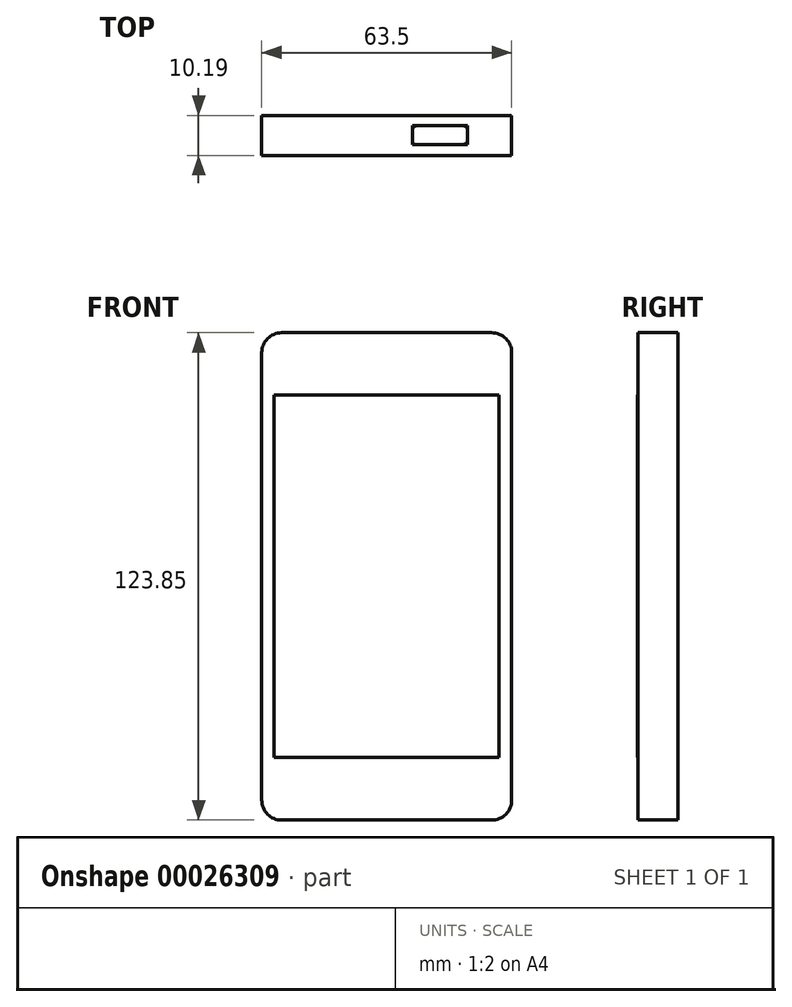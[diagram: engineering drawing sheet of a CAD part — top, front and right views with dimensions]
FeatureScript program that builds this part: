
annotation { "Feature Type Name" : "Feature", "Feature Type Description" : "" }
export const myFeature = defineFeature(function(context is Context, id is Id, definition is map)
    precondition{}
    {
        {
            var Q0;
            Q0=qCreatedBy(makeId("Front.planeOp"),FACE);
            var sketch = newSketch(context, id + "F0", { "sketchPlane" : qUnion([Q0])});
            skLineSegment(sketch, "E0.bottom", {"start": v(-42.36, 75.13) * mm, "end": v(21.14, 75.13) * mm});
            skLineSegment(sketch, "E0.top", {"start": v(-42.36, -48.7) * mm, "end": v(21.14, -48.7) * mm});
            skLineSegment(sketch, "E0.left", {"start": v(-42.36, 75.13) * mm, "end": v(-42.36, -48.7) * mm});
            skLineSegment(sketch, "E0.right", {"start": v(21.14, 75.13) * mm, "end": v(21.14, -48.7) * mm});
            skSolve(sketch);
        }
        {
            var Q0;
            Q0 = qSketchRegion(id + "F0", true);
            extrude(context, id + "F1", {"entities" : qUnion([Q0]), "depth" : 10.16 * mm});
        }
        {
            var Q0;
            Q0=makeQuery(id+"F1.opExtrude","SWEPT_EDGE",EDGE,{"disambiguationData":[OSD([sQuery(id+"F0.wireOp",EDGE,"E0.bottom"),sQuery(id+"F0.wireOp",EDGE,"E0.left")])]});
            var Q1;
            Q1=makeQuery(id+"F1.opExtrude","SWEPT_EDGE",EDGE,{"disambiguationData":[OSD([sQuery(id+"F0.wireOp",EDGE,"E0.bottom"),sQuery(id+"F0.wireOp",EDGE,"E0.right")])]});
            var Q2;
            Q2=makeQuery(id+"F1.opExtrude","SWEPT_EDGE",EDGE,{"disambiguationData":[OSD([sQuery(id+"F0.wireOp",EDGE,"E0.top"),sQuery(id+"F0.wireOp",EDGE,"E0.right")])]});
            fillet(context, id + "F2", {"entities" : qUnion([Q0, Q1, Q2]), "radius" : 5.08 * mm, "tangentPropagation" : true, "allowEdgeOverflow" : false});
        }
        {
            var Q0;
            Q0=makeQuery(id+"F1.opExtrude","SWEPT_EDGE",EDGE,{"disambiguationData":[OSD([sQuery(id+"F0.wireOp",EDGE,"E0.top"),sQuery(id+"F0.wireOp",EDGE,"E0.left")])]});
            fillet(context, id + "F3", {"entities" : qUnion([Q0]), "radius" : 5.08 * mm, "tangentPropagation" : true, "allowEdgeOverflow" : false});
        }
        {
            var Q0;
            Q0=makeQuery(id+"F1.opExtrude","CAP_FACE",FACE,{"disambiguationData":[OSD([sQuery(id+"F0.wireOp",EDGE,"E0.bottom"),sQuery(id+"F0.wireOp",EDGE,"E0.top"),sQuery(id+"F0.wireOp",EDGE,"E0.left"),sQuery(id+"F0.wireOp",EDGE,"E0.right")])],"isStart":false});
            var sketch = newSketch(context, id + "F4", { "sketchPlane" : qUnion([Q0])});
            skLineSegment(sketch, "E1.0", {"start": v(-39.18, 59.25) * mm, "end": v(17.97, 59.25) * mm});
            skLineSegment(sketch, "E2.0", {"start": v(17.97, 59.25) * mm, "end": v(17.97, -32.82) * mm});
            skLineSegment(sketch, "E3.0", {"start": v(-39.18, 59.25) * mm, "end": v(-39.18, -32.82) * mm});
            skLineSegment(sketch, "E4.0", {"start": v(-39.18, -32.82) * mm, "end": v(17.97, -32.82) * mm});
            skSolve(sketch);
        }
        {
            var Q0;
            Q0=makeQuery(id+"F4.imprint","IMPRINT",FACE,{"disambiguationData":[TD([[makeQuery(id+"F4.imprint","IMPRINT",EDGE,{"derivedFrom":sQuery(id+"F4.wireOp",EDGE,"E1.0")}),-1.0]])]});
            extrude(context, id + "F5", {"entities" : qUnion([Q0]), "depth" : 0.03 * mm});
        }
        {
            var Q0;
            Q0=makeQuery(id+"F1.opExtrude","SWEPT_FACE",FACE,{"disambiguationData":[OSD([sQuery(id+"F0.wireOp",EDGE,"E0.bottom")])]});
            var sketch = newSketch(context, id + "F6", { "sketchPlane" : qUnion([Q0])});
            skLineSegment(sketch, "E5.bottom", {"start": v(20.97, 0) * mm, "end": v(-42.15, 0) * mm, "construction": true});
            skLineSegment(sketch, "E5.top", {"start": v(20.97, -9.96) * mm, "end": v(-42.15, -9.96) * mm, "construction": true});
            skLineSegment(sketch, "E5.left", {"start": v(20.97, 0) * mm, "end": v(20.97, -9.96) * mm, "construction": true});
            skLineSegment(sketch, "E5.right", {"start": v(-42.15, 0) * mm, "end": v(-42.15, -9.96) * mm, "construction": true});
            skLineSegment(sketch, "E6.0", {"start": v(-4.05, -2.54) * mm, "end": v(-4.05, -7.42) * mm});
            skLineSegment(sketch, "E7.0", {"start": v(9.86, -2.54) * mm, "end": v(-4.05, -2.54) * mm});
            skLineSegment(sketch, "E8.0", {"start": v(9.86, -7.42) * mm, "end": v(-4.05, -7.42) * mm});
            skLineSegment(sketch, "E9.0", {"start": v(9.86, -2.54) * mm, "end": v(9.86, -7.42) * mm});
            skSolve(sketch);
        }
        {
            var Q0;
            Q0 = qSketchRegion(id + "F6", true);
            extrude(context, id + "F7", {"entities" : qUnion([Q0]), "depth" : 0.03 * mm});
        }
        {
            var Q0;
            Q0=makeQuery(id+"F7.opExtrude","CAP_EDGE",EDGE,{"disambiguationData":[OSD([sQuery(id+"F6.wireOp",EDGE,"E7.0")])],"isStart":false});
            var Q1;
            Q1=makeQuery(id+"F7.opExtrude","CAP_EDGE",EDGE,{"disambiguationData":[OSD([sQuery(id+"F6.wireOp",EDGE,"E9.0")])],"isStart":false});
            var Q2;
            Q2=makeQuery(id+"F7.opExtrude","CAP_EDGE",EDGE,{"disambiguationData":[OSD([sQuery(id+"F6.wireOp",EDGE,"E6.0")])],"isStart":false});
            var Q3;
            Q3=makeQuery(id+"F7.opExtrude","CAP_EDGE",EDGE,{"disambiguationData":[OSD([sQuery(id+"F6.wireOp",EDGE,"E8.0")])],"isStart":false});
            fillet(context, id + "F8", {"entities" : qUnion([Q0, Q1, Q2, Q3]), "radius" : 5.08 * mm, "tangentPropagation" : true, "allowEdgeOverflow" : false});
        }
    });
